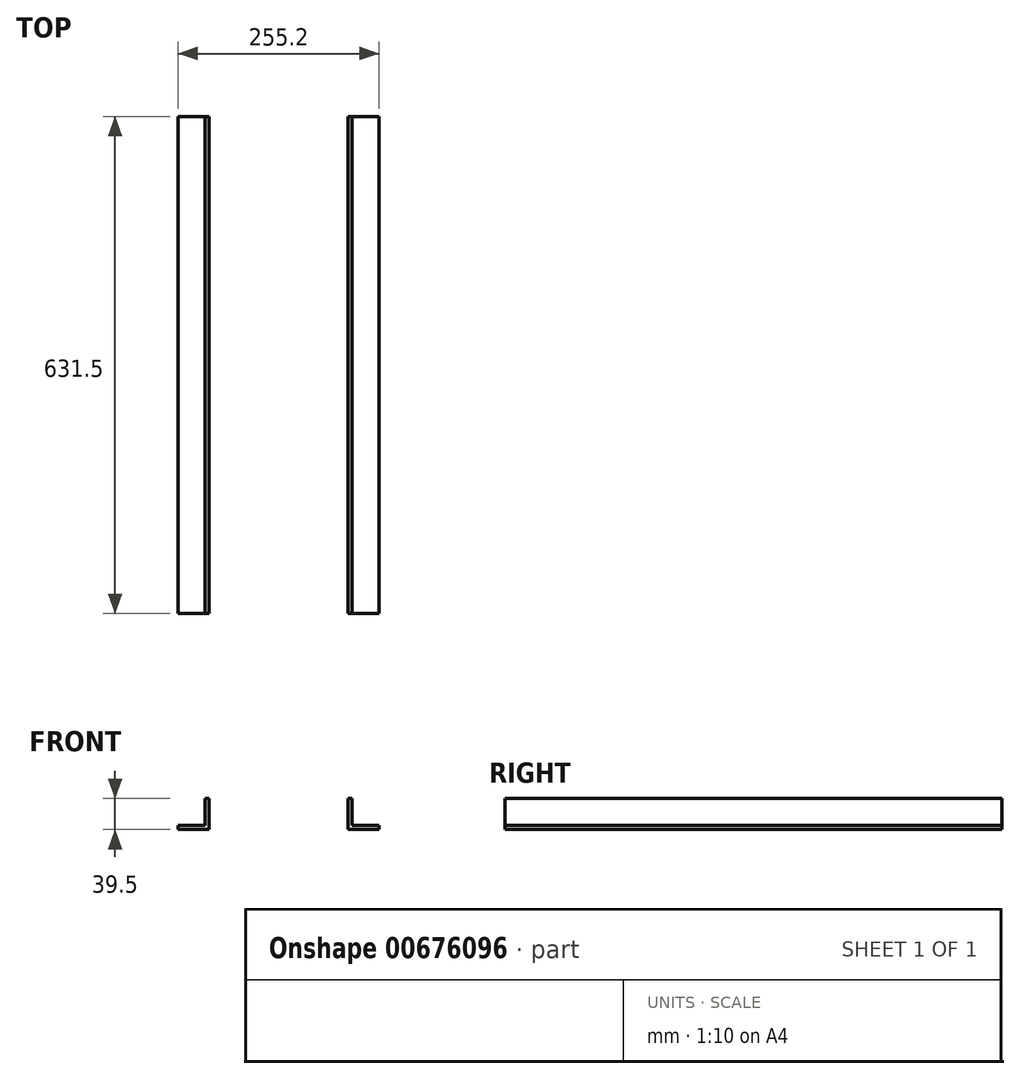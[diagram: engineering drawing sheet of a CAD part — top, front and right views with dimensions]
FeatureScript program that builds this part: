
annotation { "Feature Type Name" : "Feature", "Feature Type Description" : "" }
export const myFeature = defineFeature(function(context is Context, id is Id, definition is map)
    precondition{}
    {
        {
            var Q0;
            Q0=qCreatedBy(makeId("Front.planeOp"),FACE);
            var sketch = newSketch(context, id + "F0", { "sketchPlane" : qUnion([Q0])});
            skLineSegment(sketch, "E0", {"start": v(0, 0) * mm, "end": v(34.5, 0) * mm});
            skLineSegment(sketch, "E1", {"start": v(34.5, 0) * mm, "end": v(34.5, 34.5) * mm});
            skLineSegment(sketch, "E2", {"start": v(34.5, 34.5) * mm, "end": v(39.5, 34.5) * mm});
            skLineSegment(sketch, "E3", {"start": v(39.5, 34.5) * mm, "end": v(39.5, -5) * mm});
            skLineSegment(sketch, "E4", {"start": v(39.5, -5) * mm, "end": v(0, -5) * mm});
            skLineSegment(sketch, "E5", {"start": v(0, -5) * mm, "end": v(0, 0) * mm});
            skLineSegment(sketch, "E6", {"start": v(215.7, 34.5) * mm, "end": v(215.7, -5) * mm});
            skLineSegment(sketch, "E7", {"start": v(215.7, -5) * mm, "end": v(255.2, -5) * mm});
            skLineSegment(sketch, "E8", {"start": v(255.2, -5) * mm, "end": v(255.2, 0) * mm});
            skLineSegment(sketch, "E9", {"start": v(255.2, 0) * mm, "end": v(220.7, 0) * mm});
            skLineSegment(sketch, "E10", {"start": v(220.7, 0) * mm, "end": v(220.7, 34.5) * mm});
            skLineSegment(sketch, "E11", {"start": v(220.7, 34.5) * mm, "end": v(215.7, 34.5) * mm});
            skSolve(sketch);
        }
        {
            var Q0;
            Q0 = qSketchRegion(id + "F0", true);
            extrude(context, id + "F1", {"entities" : qUnion([Q0]), "depth" : 631.5 * mm, "offsetDistance" : 25 * mm});
        }
    });
